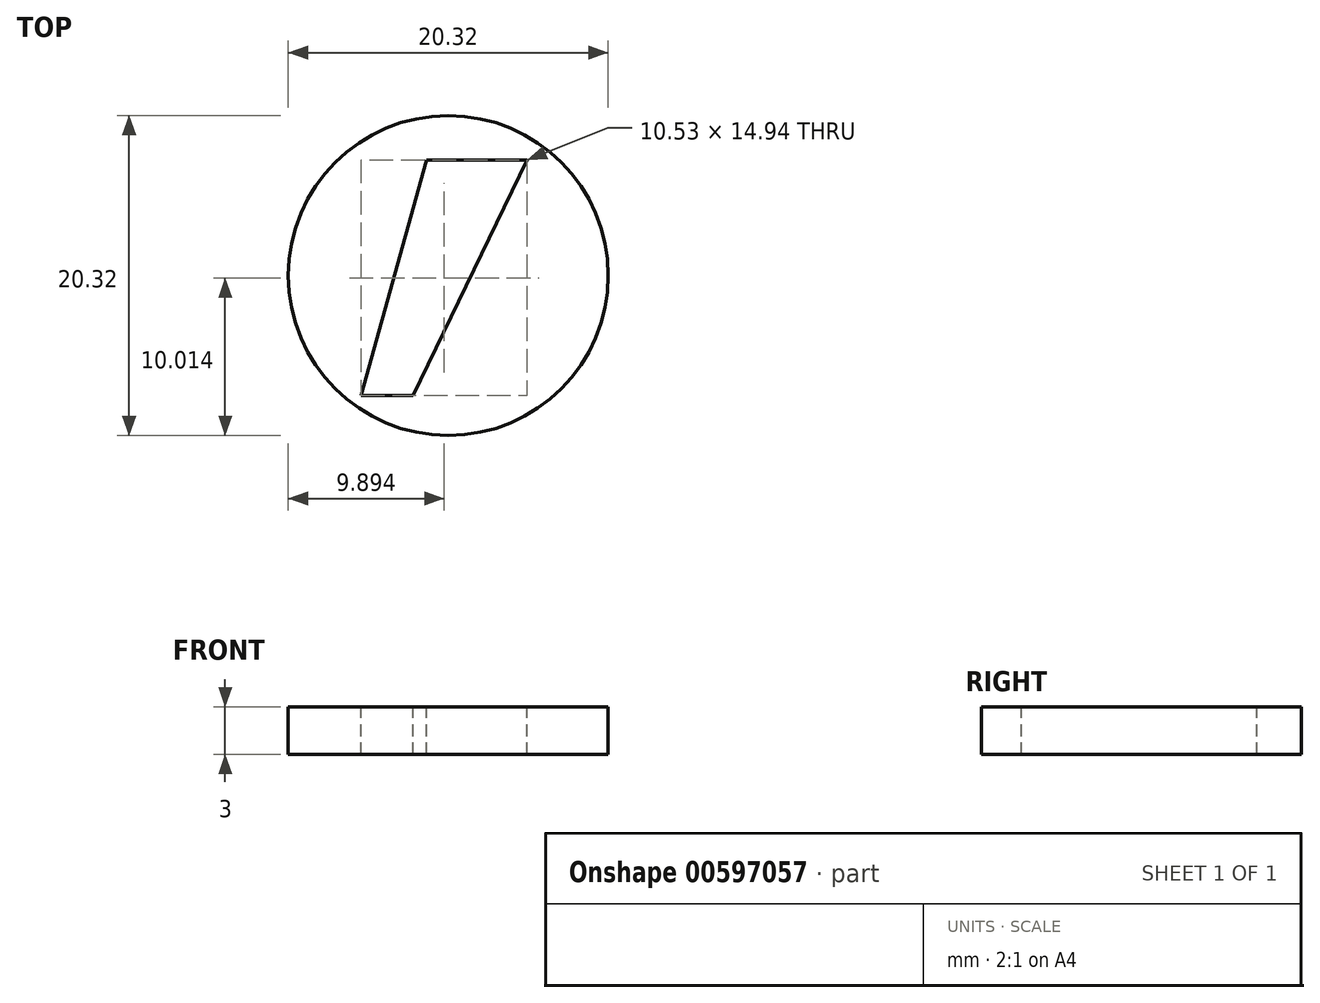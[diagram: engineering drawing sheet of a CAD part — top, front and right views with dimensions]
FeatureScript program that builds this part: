
annotation { "Feature Type Name" : "Feature", "Feature Type Description" : "" }
export const myFeature = defineFeature(function(context is Context, id is Id, definition is map)
    precondition{}
    {
        {
            var Q0;
            Q0=qCreatedBy(makeId("Top.planeOp"),FACE);
            var sketch = newSketch(context, id + "F0", { "sketchPlane" : qUnion([Q0])});
            skCircle(sketch, "E0", {"center": v(0, 0) * mm, "radius": 10.16 * mm});
            skSolve(sketch);
        }
        {
            var Q0;
            Q0 = qSketchRegion(id + "F0", true);
            extrude(context, id + "F1", {"entities" : qUnion([Q0]), "depth" : 3 * mm, "offsetDistance" : 25.4 * mm});
        }
        {
            var Q0;
            Q0=makeQuery(id+"F1.opExtrude","CAP_FACE",FACE,{"disambiguationData":[OSD([sQuery(id+"F0.wireOp",EDGE,"E0")])],"isStart":false});
            var sketch = newSketch(context, id + "F2", { "sketchPlane" : qUnion([Q0])});
            skLineSegment(sketch, "E1", {"start": v(-5.53, -7.62) * mm, "end": v(-1.37, 7.33) * mm});
            skLineSegment(sketch, "E2", {"start": v(-1.37, 7.33) * mm, "end": v(5, 7.33) * mm});
            skLineSegment(sketch, "E3", {"start": v(5, 7.33) * mm, "end": v(-2.24, -7.62) * mm});
            skLineSegment(sketch, "E4", {"start": v(-5.53, -7.62) * mm, "end": v(-2.24, -7.62) * mm});
            skPoint(sketch, "E5.orphan", {"position": v(0, -7.62) * mm});
            skSolve(sketch);
        }
        {
            var Q0;
            Q0 = qSketchRegion(id + "F2", true);
            extrude(context, id + "F3", {"entities" : qUnion([Q0]), "operationType" : NewBodyOperationType.REMOVE, "oppositeDirection" : true, "depth" : 25.4 * mm, "offsetDistance" : 25.4 * mm});
        }
    });
